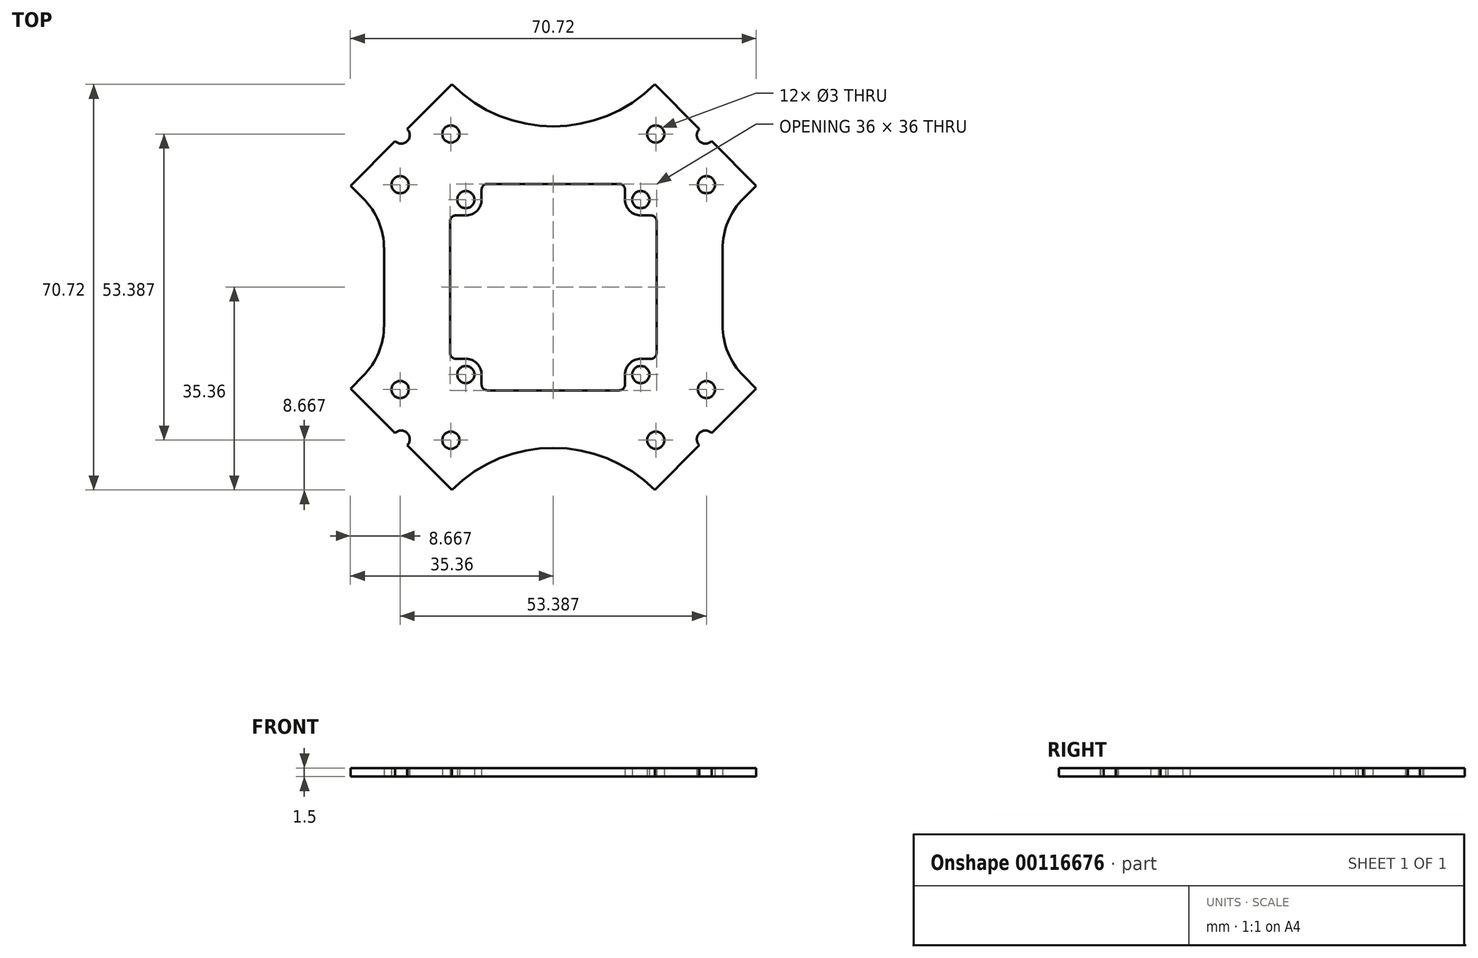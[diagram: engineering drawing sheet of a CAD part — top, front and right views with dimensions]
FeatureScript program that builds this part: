
annotation { "Feature Type Name" : "Feature", "Feature Type Description" : "" }
export const myFeature = defineFeature(function(context is Context, id is Id, definition is map)
    precondition{}
    {
        {
            var Q0;
            Q0=qCreatedBy(makeId("Top.planeOp"),FACE);
            var sketch = newSketch(context, id + "F0", { "sketchPlane" : qUnion([Q0])});
            skLineSegment(sketch, "E0", {"start": v(-11.5, -18) * mm, "end": v(11.5, -18) * mm});
            skArc(sketch, "E1", {"start": v(-12.5, -17) * mm, "mid": v(-12.2, -17.7) * mm, "end": v(-11.5, -18) * mm});
            skLineSegment(sketch, "E2", {"start": v(18, -11.5) * mm, "end": v(18, 11.5) * mm});
            skLineSegment(sketch, "E3", {"start": v(-18, 11.5) * mm, "end": v(-18, -11.5) * mm});
            skArc(sketch, "E4", {"start": v(-18, -11.5) * mm, "mid": v(-17.7, -12.2) * mm, "end": v(-17, -12.5) * mm});
            skCircle(sketch, "E5", {"center": v(-15.25, -15.25) * mm, "radius": 1.5 * mm});
            skArc(sketch, "E6", {"start": v(-12.5, -15.25) * mm, "mid": v(-13.3, -13.3) * mm, "end": v(-15.25, -12.5) * mm});
            skLineSegment(sketch, "E7", {"start": v(-12.5, -15.25) * mm, "end": v(-12.5, -17) * mm});
            skLineSegment(sketch, "E8", {"start": v(-15.25, -12.5) * mm, "end": v(-17, -12.5) * mm});
            skArc(sketch, "E9", {"start": v(17, -12.5) * mm, "mid": v(17.7, -12.2) * mm, "end": v(18, -11.5) * mm});
            skArc(sketch, "E10", {"start": v(11.5, -18) * mm, "mid": v(12.2, -17.7) * mm, "end": v(12.5, -17) * mm});
            skCircle(sketch, "E11", {"center": v(15.25, -15.25) * mm, "radius": 1.5 * mm});
            skArc(sketch, "E12", {"start": v(15.25, -12.5) * mm, "mid": v(13.3, -13.3) * mm, "end": v(12.5, -15.25) * mm});
            skLineSegment(sketch, "E13", {"start": v(15.25, -12.5) * mm, "end": v(17, -12.5) * mm});
            skLineSegment(sketch, "E14", {"start": v(12.5, -15.25) * mm, "end": v(12.5, -17) * mm});
            skArc(sketch, "E15", {"start": v(12.5, 17) * mm, "mid": v(12.2, 17.7) * mm, "end": v(11.5, 18) * mm});
            skArc(sketch, "E16", {"start": v(18, 11.5) * mm, "mid": v(17.7, 12.2) * mm, "end": v(17, 12.5) * mm});
            skCircle(sketch, "E17", {"center": v(15.25, 15.25) * mm, "radius": 1.5 * mm});
            skArc(sketch, "E18", {"start": v(12.5, 15.25) * mm, "mid": v(13.3, 13.3) * mm, "end": v(15.25, 12.5) * mm});
            skLineSegment(sketch, "E19", {"start": v(12.5, 15.25) * mm, "end": v(12.5, 17) * mm});
            skLineSegment(sketch, "E20", {"start": v(15.25, 12.5) * mm, "end": v(17, 12.5) * mm});
            skArc(sketch, "E21", {"start": v(-17, 12.5) * mm, "mid": v(-17.7, 12.2) * mm, "end": v(-18, 11.5) * mm});
            skArc(sketch, "E22", {"start": v(-11.5, 18) * mm, "mid": v(-12.2, 17.7) * mm, "end": v(-12.5, 17) * mm});
            skCircle(sketch, "E23", {"center": v(-15.25, 15.25) * mm, "radius": 1.5 * mm});
            skArc(sketch, "E24", {"start": v(-15.25, 12.5) * mm, "mid": v(-13.3, 13.3) * mm, "end": v(-12.5, 15.25) * mm});
            skLineSegment(sketch, "E25", {"start": v(-15.25, 12.5) * mm, "end": v(-17, 12.5) * mm});
            skLineSegment(sketch, "E26", {"start": v(-12.5, 15.25) * mm, "end": v(-12.5, 17) * mm});
            skLineSegment(sketch, "E27", {"start": v(-11.5, 18) * mm, "end": v(11.5, 18) * mm});
            skLineSegment(sketch, "E28", {"start": v(-29.5, 0) * mm, "end": v(-29.5, -6.64) * mm});
            skArc(sketch, "E29", {"start": v(-33.16, -15.48) * mm, "mid": v(-30.45, -11.43) * mm, "end": v(-29.5, -6.64) * mm});
            skLineSegment(sketch, "E30", {"start": v(29.5, 0) * mm, "end": v(29.5, -6.64) * mm});
            skArc(sketch, "E31", {"start": v(29.5, -6.64) * mm, "mid": v(30.45, -11.43) * mm, "end": v(33.16, -15.48) * mm});
            skLineSegment(sketch, "E32", {"start": v(-29.5, 0) * mm, "end": v(-29.5, 6.64) * mm});
            skLineSegment(sketch, "E33", {"start": v(29.5, 0) * mm, "end": v(29.5, 6.64) * mm});
            skArc(sketch, "E34", {"start": v(33.16, 15.48) * mm, "mid": v(30.45, 11.43) * mm, "end": v(29.5, 6.64) * mm});
            skArc(sketch, "E35", {"start": v(-17.68, 35.36) * mm, "mid": v(0, 28.03) * mm, "end": v(17.68, 35.36) * mm});
            skArc(sketch, "E36", {"start": v(-29.5, 6.64) * mm, "mid": v(-30.45, 11.43) * mm, "end": v(-33.16, 15.48) * mm});
            skArc(sketch, "E37", {"start": v(17.68, -35.36) * mm, "mid": v(0, -28.03) * mm, "end": v(-17.68, -35.36) * mm});
            skLineSegment(sketch, "E38", {"start": v(-17.68, 35.36) * mm, "end": v(-25.46, 27.58) * mm});
            skLineSegment(sketch, "E39", {"start": v(-27.58, 25.46) * mm, "end": v(-35.36, 17.68) * mm});
            skCircle(sketch, "E40", {"center": v(-26.7, -17.85) * mm, "radius": 1.5 * mm});
            skCircle(sketch, "E41", {"center": v(-17.85, -26.7) * mm, "radius": 1.5 * mm});
            skCircle(sketch, "E42", {"center": v(17.85, -26.7) * mm, "radius": 1.5 * mm});
            skCircle(sketch, "E43", {"center": v(26.7, -17.85) * mm, "radius": 1.5 * mm});
            skCircle(sketch, "E44", {"center": v(26.7, 17.85) * mm, "radius": 1.5 * mm});
            skCircle(sketch, "E45", {"center": v(17.85, 26.7) * mm, "radius": 1.5 * mm});
            skCircle(sketch, "E46", {"center": v(-17.85, 26.7) * mm, "radius": 1.5 * mm});
            skCircle(sketch, "E47", {"center": v(-26.7, 17.85) * mm, "radius": 1.5 * mm});
            skLineSegment(sketch, "E48", {"start": v(33.16, -15.48) * mm, "end": v(35.36, -17.68) * mm});
            skLineSegment(sketch, "E49", {"start": v(33.16, 15.48) * mm, "end": v(35.36, 17.68) * mm});
            skLineSegment(sketch, "E50", {"start": v(-33.16, 15.48) * mm, "end": v(-35.36, 17.68) * mm});
            skLineSegment(sketch, "E51", {"start": v(-35.36, -17.68) * mm, "end": v(-33.16, -15.48) * mm});
            skArc(sketch, "E52", {"start": v(-27.58, 25.46) * mm, "mid": v(-25.46, 25.46) * mm, "end": v(-25.46, 27.58) * mm});
            skLineSegment(sketch, "E53", {"start": v(-35.36, -17.68) * mm, "end": v(-27.58, -25.46) * mm});
            skLineSegment(sketch, "E54", {"start": v(-25.46, -27.58) * mm, "end": v(-17.68, -35.36) * mm});
            skArc(sketch, "E55", {"start": v(-25.46, -27.58) * mm, "mid": v(-25.46, -25.46) * mm, "end": v(-27.58, -25.46) * mm});
            skLineSegment(sketch, "E56", {"start": v(17.68, -35.36) * mm, "end": v(25.46, -27.58) * mm});
            skLineSegment(sketch, "E57", {"start": v(27.58, -25.46) * mm, "end": v(35.36, -17.68) * mm});
            skArc(sketch, "E58", {"start": v(27.58, -25.46) * mm, "mid": v(25.46, -25.46) * mm, "end": v(25.46, -27.58) * mm});
            skLineSegment(sketch, "E59", {"start": v(35.36, 17.68) * mm, "end": v(27.58, 25.46) * mm});
            skLineSegment(sketch, "E60", {"start": v(25.46, 27.58) * mm, "end": v(17.68, 35.36) * mm});
            skArc(sketch, "E61", {"start": v(25.46, 27.58) * mm, "mid": v(25.46, 25.46) * mm, "end": v(27.58, 25.46) * mm});
            skSolve(sketch);
        }
        {
            var Q0;
            Q0 = qSketchRegion(id + "F0", true);
            extrude(context, id + "F1", {"entities" : qUnion([Q0]), "depth" : 1.5 * mm});
        }
    });
